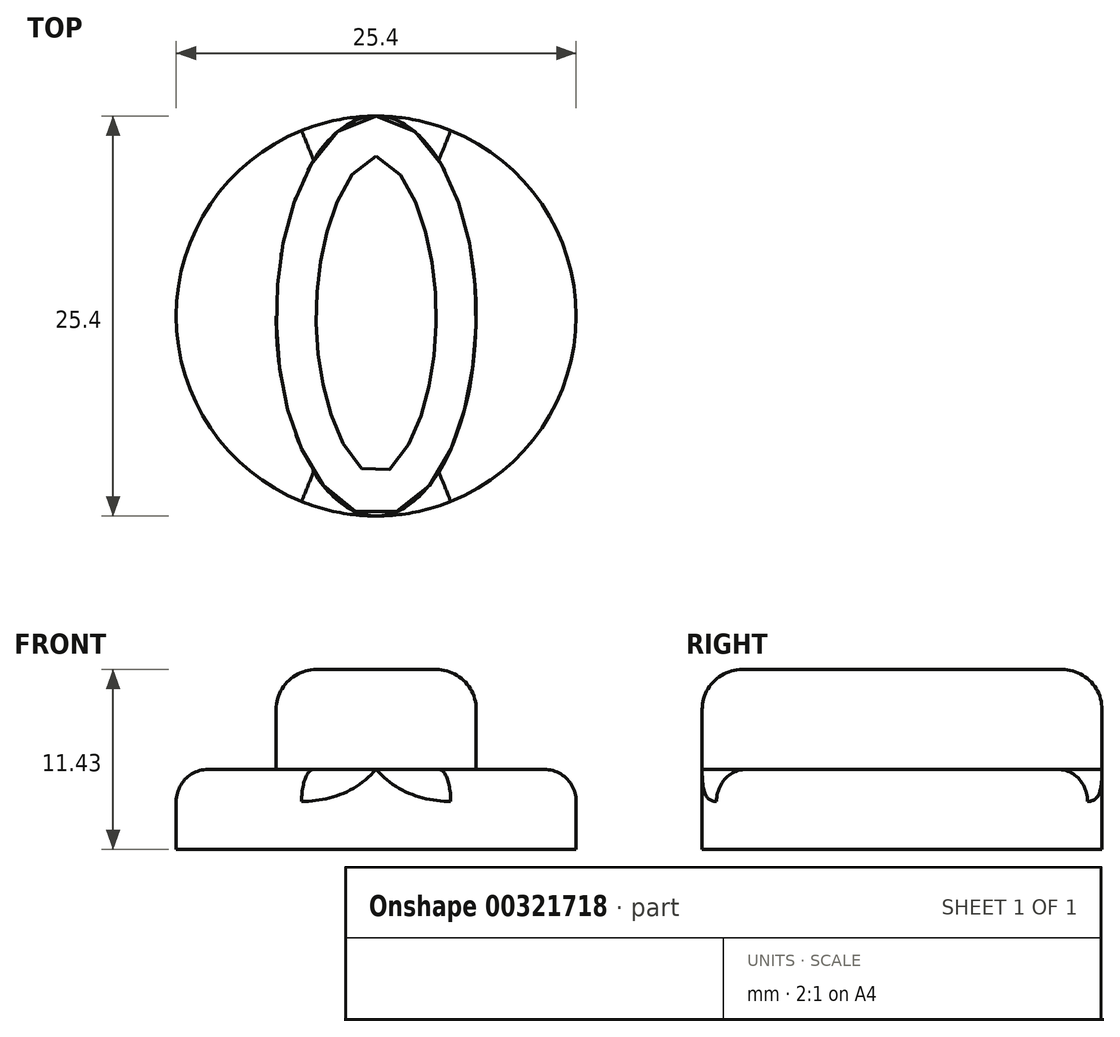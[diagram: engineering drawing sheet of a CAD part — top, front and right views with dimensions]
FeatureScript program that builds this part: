
annotation { "Feature Type Name" : "Feature", "Feature Type Description" : "" }
export const myFeature = defineFeature(function(context is Context, id is Id, definition is map)
    precondition{}
    {
        {
            var Q0;
            Q0=qCreatedBy(makeId("Top.planeOp"),FACE);
            var sketch = newSketch(context, id + "F0", { "sketchPlane" : qUnion([Q0])});
            skCircle(sketch, "E0", {"center": v(0, 0) * mm, "radius": 12.7 * mm});
            skSolve(sketch);
        }
        {
            var Q0;
            Q0=makeQuery(id+"F0.imprint","IMPRINT",FACE,{"disambiguationData":[TD([[makeQuery(id+"F0.imprint","IMPRINT",EDGE,{"derivedFrom":sQuery(id+"F0.wireOp",EDGE,"E0")}),1.0]])]});
            extrude(context, id + "F1", {"entities" : qUnion([Q0]), "depth" : 5.08 * mm});
        }
        {
            var Q0;
            Q0=makeQuery(id+"F1.opExtrude","CAP_FACE",FACE,{"disambiguationData":[OSD([sQuery(id+"F0.wireOp",EDGE,"E0")])],"isStart":false});
            var sketch = newSketch(context, id + "F2", { "sketchPlane" : qUnion([Q0])});
            skEllipse(sketch, "E1", {"center": v(0, 0) * mm, "majorRadius": 12.7 * mm, "minorRadius": 6.35 * mm, "majorAxis": v(0, 1)});
            skSolve(sketch);
        }
        {
            var Q0;
            {var subQ0=sQuery(id+"F2.wireOp",EDGE,"E1");var subQ1=makeQuery(id+"F1.opExtrude","CAP_EDGE",EDGE,{"disambiguationData":[OSD([sQuery(id+"F0.wireOp",EDGE,"E0")])],"isStart":false});var subQ2=makeQuery(id+"F2.imprint","INTERSECT",VERTEX,{"disambiguationData":[OD(0.0)],"derivedFrom":[subQ1,subQ0]});Q0=makeQuery(id+"F2.imprint","IMPRINT",FACE,{"disambiguationData":[TD([[makeQuery(id+"F2.imprint","IMPRINT",EDGE,{"disambiguationData":[TD([[subQ2,1.0]])],"derivedFrom":subQ0}),1.0]])]});}
            extrude(context, id + "F3", {"entities" : qUnion([Q0]), "operationType" : NewBodyOperationType.ADD, "depth" : 6.35 * mm});
        }
        {
            var Q0;
            Q0=makeQuery(id+"F3.opExtrude","CAP_EDGE",EDGE,{"disambiguationData":[OSD([sQuery(id+"F2.wireOp",EDGE,"E1")])],"isStart":false});
            fillet(context, id + "F4", {"entities" : qUnion([Q0]), "radius" : 2.54 * mm, "tangentPropagation" : true, "allowEdgeOverflow" : false});
        }
        {
            var Q0;
            Q0=makeQuery(id+"F3.boolean.opBoolean","SPLIT",EDGE,{"disambiguationData":[OD(0.0)],"derivedFrom":makeQuery(id+"F1.opExtrude","CAP_EDGE",EDGE,{"disambiguationData":[OSD([sQuery(id+"F0.wireOp",EDGE,"E0")])],"isStart":false})});
            var Q1;
            Q1=makeQuery(id+"F3.boolean.opBoolean","SPLIT",EDGE,{"disambiguationData":[OD(1.0)],"derivedFrom":makeQuery(id+"F1.opExtrude","CAP_EDGE",EDGE,{"disambiguationData":[OSD([sQuery(id+"F0.wireOp",EDGE,"E0")])],"isStart":false})});
            fillet(context, id + "F5", {"entities" : qUnion([Q0, Q1]), "radius" : 2.03 * mm, "tangentPropagation" : true, "allowEdgeOverflow" : false});
        }
    });
